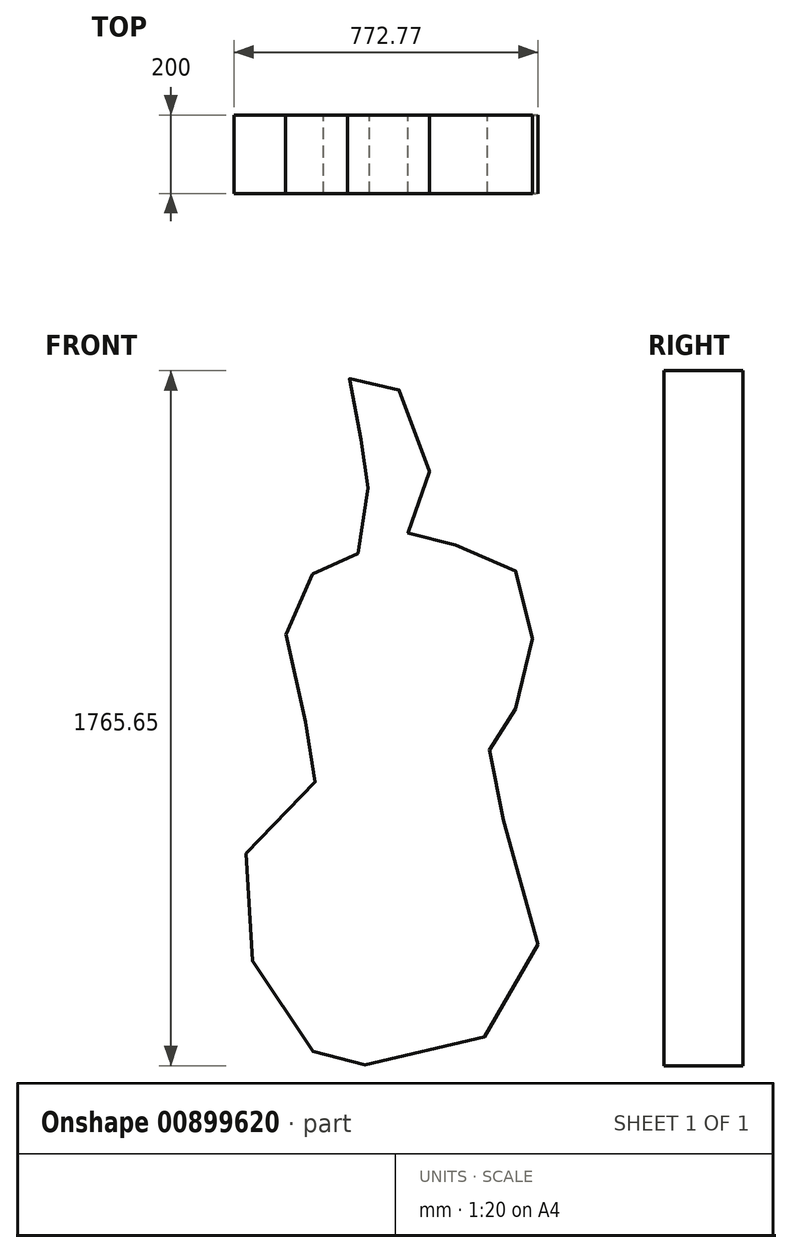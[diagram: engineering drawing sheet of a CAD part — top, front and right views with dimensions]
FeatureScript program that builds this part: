
annotation { "Feature Type Name" : "Feature", "Feature Type Description" : "" }
export const myFeature = defineFeature(function(context is Context, id is Id, definition is map)
    precondition{}
    {
        {
            var Q0;
            Q0=qCreatedBy(makeId("Front.planeOp"),FACE);
            var sketch = newSketch(context, id + "F0", { "sketchPlane" : qUnion([Q0])});
            skLineSegment(sketch, "E0", {"start": v(0, 0) * mm, "end": v(0, 1750) * mm, "construction": true});
            skFitSpline(sketch, "E1", {"points": [v(-57.8, 1590.48) * mm, v(-87.86, 1744.48) * mm, v(0, 1750) * mm, v(114.97, 1500.34) * mm, v(62.38, 1350.1) * mm, v(137.5, 1327.56) * mm, v(314.04, 1278.73) * mm, v(377.9, 1109.7) * mm, v(332.82, 903.12) * mm, v(276.48, 820.5) * mm, v(276.48, 704.05) * mm, v(362.87, 163.18) * mm, v(-106.64, 0) * mm, v(-178, 35.48) * mm, v(-377.07, 471.18) * mm, v(-155.47, 752.88) * mm, v(-230.59, 936.93) * mm, v(-211.8, 1222.39) * mm, v(-132.93, 1263.7) * mm, v(-46.54, 1331.32) * mm, v(-46.54, 1519.12) * mm, v(-57.8, 1590.48) * mm]});
            skSolve(sketch);
        }
        {
            var Q0;
            Q0 = qSketchRegion(id + "F0", true);
            extrude(context, id + "F1", {"entities" : qUnion([Q0]), "depth" : 200 * mm, "offsetDistance" : 25 * mm});
        }
    });
